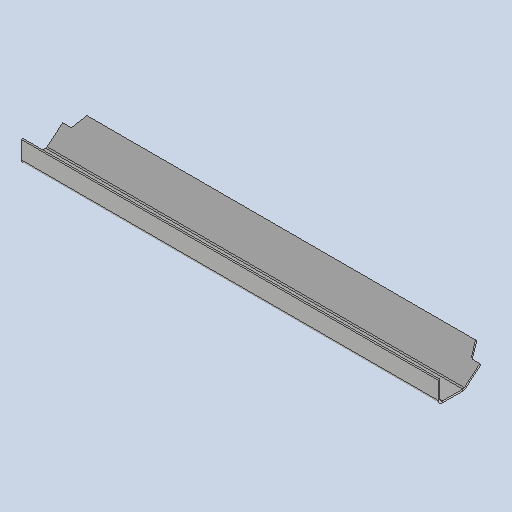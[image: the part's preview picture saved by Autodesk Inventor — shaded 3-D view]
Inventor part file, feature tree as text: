
AUTODESK INVENTOR PART (.ipt)
format: ipt  version: 2025 (Build 290162010, 162A)  size: 306,176 bytes
history: native  units: mm
features: sheet_metal_op x9, other x7, sketch x5
ambient origin geometry x8: Origin, YZ Plane, XZ Plane, XY Plane, X Axis, Y Axis, Z Axis, Center Point
bodies: Solid1 (feature_tree)
feature tree (21):
  sheet_metal_op  "Face1"
  other  "Mark1"
  other  "A-Side Definition"
  sheet_metal_op  "Flange1"
  sheet_metal_op  "Flange2"
  sheet_metal_op  "Face2"
  sketch  "Sketch1"  dims[d0=480.0mm]
  other  "Plate1"
  sketch  "Sketch2"  dims[d1=30.0mm]
  sketch  "Sketch3"  dims[d2=2.0mm]
  other  "Plate2"
  sheet_metal_op  "Bend1"
  sheet_metal_op  "Corner1"
  sketch  "Sketch4"  dims[d6=200.0mm]
  other  "Plate3"
  sheet_metal_op  "Bend2"
  sheet_metal_op  "Corner2"
  sketch  "Sketch5"  dims[d9=20.0mm d10=10.0mm d11=20.0mm d12=2.0mm d13=1.0mm d14=4.0mm d15=2.75mm d16=25.0mm d17=90.0deg d18=2.75mm d19=8.0mm d20=2.0mm d21=2.75mm d22=2.0mm d23=1.0mm d24=4.0mm d25=2.75mm d26=25.0mm d27=6.981317mm d28=2.75mm d29=8.0mm d30=2.0mm d31=2.75mm d32=10.0mm d33=15.0mm d34=2.75mm d35=2.0mm d36=1.0mm d37=4.0mm d38=2.75mm]
  other  "Plate4"
  sheet_metal_op  "Bend3"
  other  "Definition1"
